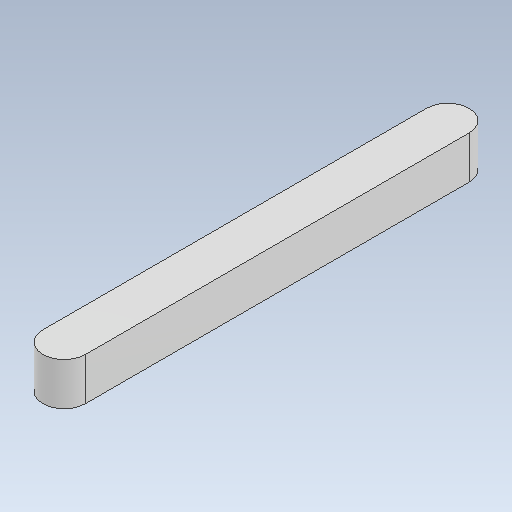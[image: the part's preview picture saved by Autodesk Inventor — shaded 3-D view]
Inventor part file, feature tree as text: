
AUTODESK INVENTOR PART (.ipt)
format: ipt  version: 2020 (Build 240168000, 168)  size: 82,432 bytes
history: native  units: in
note: dims shown in document units (in); Inventor stores cm internally (conversion verified against a paired STEP export)
features: fillet x1
ambient origin geometry x8: Origin, YZ Plane, XZ Plane, XY Plane, X Axis, Y Axis, Z Axis, Center Point
bodies: Solid1 (feature_tree)
feature tree (1):
  fillet  "Fillet1"  [1 undecoded]
note: 1 required parameter value undecoded (feature->parameter linkage not recoverable at this tier; creation-order binding heuristic only, values carry confidence <= 0.55)
